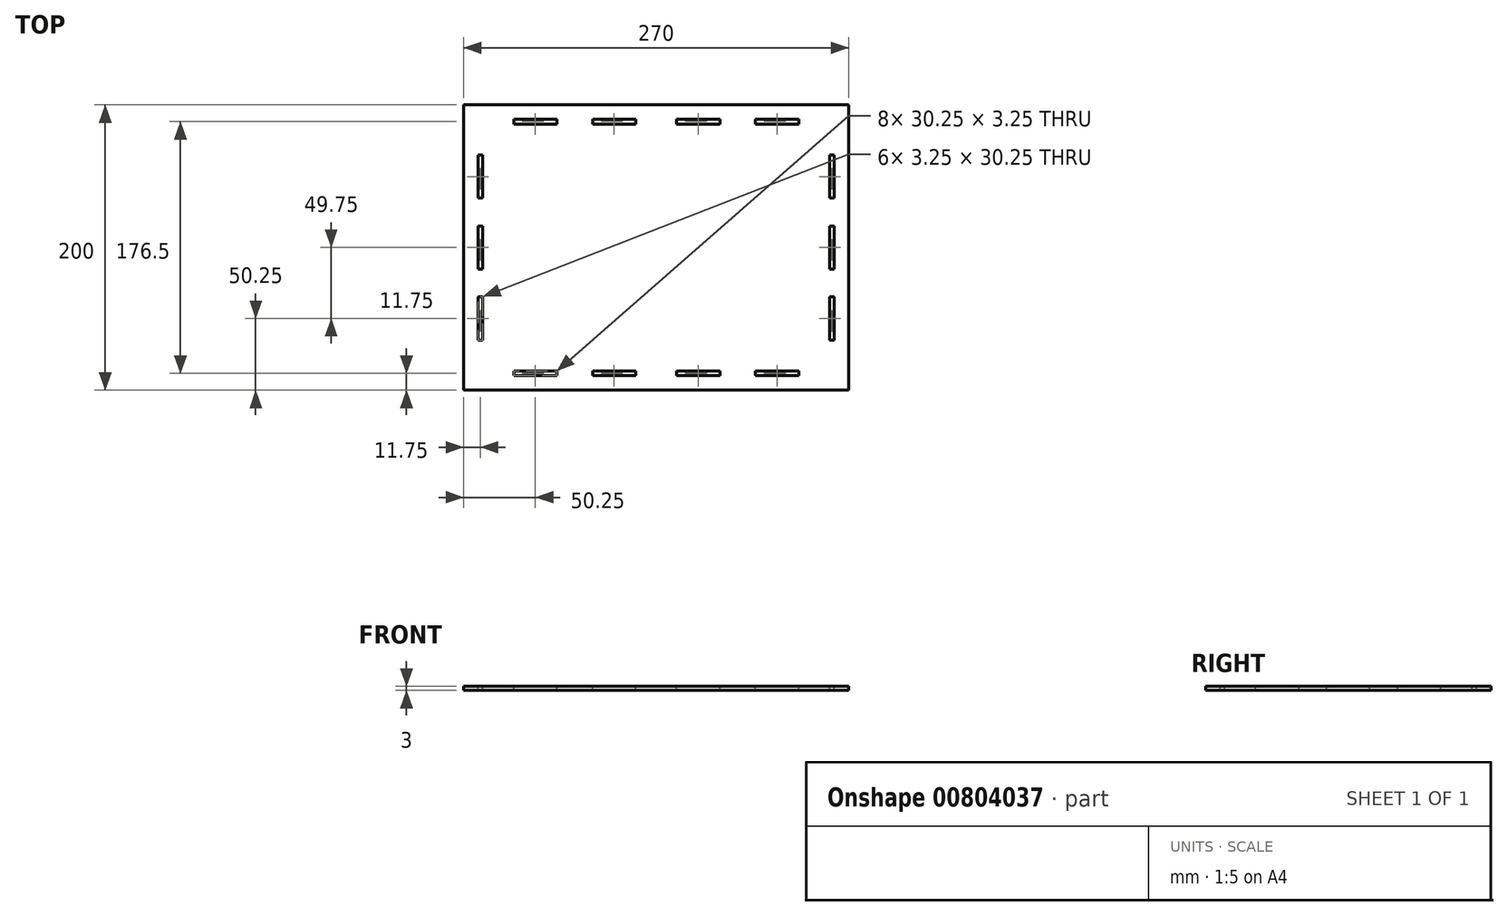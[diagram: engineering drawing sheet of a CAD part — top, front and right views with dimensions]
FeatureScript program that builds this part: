
annotation { "Feature Type Name" : "Feature", "Feature Type Description" : "" }
export const myFeature = defineFeature(function(context is Context, id is Id, definition is map)
    precondition{}
    {
        {
            var Q0;
            Q0=qCreatedBy(makeId("Top.planeOp"),FACE);
            var sketch = newSketch(context, id + "F0", { "sketchPlane" : qUnion([Q0])});
            skLineSegment(sketch, "E0.bottom", {"start": v(-135, 100) * mm, "end": v(135, 100) * mm});
            skLineSegment(sketch, "E0.top", {"start": v(-135, -100) * mm, "end": v(135, -100) * mm});
            skLineSegment(sketch, "E0.left", {"start": v(-135, 100) * mm, "end": v(-135, -100) * mm});
            skLineSegment(sketch, "E0.right", {"start": v(135, 100) * mm, "end": v(135, -100) * mm});
            skPoint(sketch, "E0.middle", {"position": v(0, 0) * mm});
            skSolve(sketch);
        }
        {
            var Q0;
            Q0=makeQuery(id+"F0.imprint","IMPRINT",FACE,{"disambiguationData":[TD([[makeQuery(id+"F0.imprint","IMPRINT",EDGE,{"derivedFrom":sQuery(id+"F0.wireOp",EDGE,"E0.bottom")}),-1.0]])]});
            extrude(context, id + "F1", {"entities" : qUnion([Q0]), "depth" : 3 * mm, "offsetDistance" : 25 * mm});
        }
        {
            var Q0;
            Q0=makeQuery(id+"F1.opExtrude","CAP_FACE",FACE,{"disambiguationData":[OSD([sQuery(id+"F0.wireOp",EDGE,"E0.bottom"),sQuery(id+"F0.wireOp",EDGE,"E0.top"),sQuery(id+"F0.wireOp",EDGE,"E0.left"),sQuery(id+"F0.wireOp",EDGE,"E0.right")])],"isStart":false});
            var sketch = newSketch(context, id + "F2", { "sketchPlane" : qUnion([Q0])});
            skLineSegment(sketch, "E1.bottom", {"start": v(-99.88, -86.63) * mm, "end": v(-69.63, -86.63) * mm});
            skLineSegment(sketch, "E1.top", {"start": v(-99.88, -89.88) * mm, "end": v(-69.63, -89.88) * mm});
            skLineSegment(sketch, "E1.left", {"start": v(-99.88, -86.63) * mm, "end": v(-99.88, -89.88) * mm});
            skLineSegment(sketch, "E1.right", {"start": v(-69.63, -86.63) * mm, "end": v(-69.63, -89.88) * mm});
            skPoint(sketch, "E1.middle", {"position": v(-84.75, -88.25) * mm});
            skLineSegment(sketch, "E2.bottom", {"start": v(-14.38, -86.62) * mm, "end": v(-44.63, -86.62) * mm});
            skLineSegment(sketch, "E2.top", {"start": v(-14.38, -89.88) * mm, "end": v(-44.63, -89.88) * mm});
            skLineSegment(sketch, "E2.left", {"start": v(-14.38, -86.62) * mm, "end": v(-14.38, -89.87) * mm});
            skLineSegment(sketch, "E2.right", {"start": v(-44.63, -86.62) * mm, "end": v(-44.63, -89.87) * mm});
            skPoint(sketch, "E2.middle", {"position": v(-29.5, -88.25) * mm});
            skLineSegment(sketch, "E3.bottom", {"start": v(121.63, 64.88) * mm, "end": v(124.88, 64.88) * mm});
            skLineSegment(sketch, "E3.top", {"start": v(121.63, 34.63) * mm, "end": v(124.88, 34.63) * mm});
            skLineSegment(sketch, "E3.left", {"start": v(121.63, 64.88) * mm, "end": v(121.63, 34.63) * mm});
            skLineSegment(sketch, "E3.right", {"start": v(124.88, 64.88) * mm, "end": v(124.88, 34.63) * mm});
            skPoint(sketch, "E3.middle", {"position": v(123.25, 49.75) * mm});
            skLineSegment(sketch, "E4.bottom", {"start": v(121.63, 15.12) * mm, "end": v(124.88, 15.12) * mm});
            skLineSegment(sketch, "E4.top", {"start": v(121.63, -15.13) * mm, "end": v(124.88, -15.13) * mm});
            skLineSegment(sketch, "E4.left", {"start": v(121.63, 15.12) * mm, "end": v(121.63, -15.13) * mm});
            skLineSegment(sketch, "E4.right", {"start": v(124.88, 15.12) * mm, "end": v(124.88, -15.13) * mm});
            skPoint(sketch, "E4.middle", {"position": v(123.25, 0) * mm});
            skLineSegment(sketch, "E5.MirrorCS", {"start": v(-69.63, 86.63) * mm, "end": v(-69.63, 89.88) * mm});
            skLineSegment(sketch, "E6.MirrorCS", {"start": v(-99.88, 86.63) * mm, "end": v(-99.88, 89.88) * mm});
            skLineSegment(sketch, "E7.MirrorCS", {"start": v(-44.63, 86.62) * mm, "end": v(-44.63, 89.87) * mm});
            skLineSegment(sketch, "E8.MirrorCS", {"start": v(-14.38, 86.62) * mm, "end": v(-14.38, 89.87) * mm});
            skLineSegment(sketch, "E9.MirrorCS", {"start": v(-14.38, 86.62) * mm, "end": v(-44.63, 86.62) * mm});
            skLineSegment(sketch, "E10.MirrorCS", {"start": v(-99.88, 89.88) * mm, "end": v(-69.63, 89.88) * mm});
            skLineSegment(sketch, "E11.MirrorCS", {"start": v(-99.88, 86.63) * mm, "end": v(-69.63, 86.63) * mm});
            skLineSegment(sketch, "E12.MirrorCS", {"start": v(-14.38, 89.88) * mm, "end": v(-44.63, 89.88) * mm});
            skPoint(sketch, "E13.MirrorP", {"position": v(-84.75, 88.25) * mm});
            skPoint(sketch, "E14.MirrorP", {"position": v(-29.5, 88.25) * mm});
            skLineSegment(sketch, "E15.MirrorCS", {"start": v(14.38, -86.62) * mm, "end": v(14.38, -89.87) * mm});
            skLineSegment(sketch, "E16.MirrorCS", {"start": v(69.63, -86.63) * mm, "end": v(69.63, -89.88) * mm});
            skLineSegment(sketch, "E17.MirrorCS", {"start": v(99.88, 86.63) * mm, "end": v(99.88, 89.88) * mm});
            skLineSegment(sketch, "E18.MirrorCS", {"start": v(14.38, 86.62) * mm, "end": v(14.38, 89.87) * mm});
            skLineSegment(sketch, "E19.MirrorCS", {"start": v(44.63, -86.62) * mm, "end": v(44.63, -89.87) * mm});
            skLineSegment(sketch, "E20.MirrorCS", {"start": v(99.88, -86.63) * mm, "end": v(99.88, -89.88) * mm});
            skLineSegment(sketch, "E21.MirrorCS", {"start": v(69.63, 86.63) * mm, "end": v(69.63, 89.88) * mm});
            skLineSegment(sketch, "E22.MirrorCS", {"start": v(44.63, 86.62) * mm, "end": v(44.63, 89.87) * mm});
            skLineSegment(sketch, "E23.MirrorCS", {"start": v(14.38, -89.88) * mm, "end": v(44.63, -89.88) * mm});
            skLineSegment(sketch, "E24.MirrorCS", {"start": v(99.88, -89.88) * mm, "end": v(69.63, -89.88) * mm});
            skLineSegment(sketch, "E25.MirrorCS", {"start": v(14.38, -86.62) * mm, "end": v(44.63, -86.62) * mm});
            skLineSegment(sketch, "E26.MirrorCS", {"start": v(14.38, 89.88) * mm, "end": v(44.63, 89.88) * mm});
            skLineSegment(sketch, "E27.MirrorCS", {"start": v(99.88, 89.88) * mm, "end": v(69.63, 89.88) * mm});
            skPoint(sketch, "E28.MirrorP", {"position": v(84.75, -88.25) * mm});
            skLineSegment(sketch, "E29.MirrorCS", {"start": v(99.88, 86.63) * mm, "end": v(69.63, 86.63) * mm});
            skLineSegment(sketch, "E30.MirrorCS", {"start": v(99.88, -86.63) * mm, "end": v(69.63, -86.63) * mm});
            skLineSegment(sketch, "E31.MirrorCS", {"start": v(14.38, 86.62) * mm, "end": v(44.63, 86.62) * mm});
            skPoint(sketch, "E32.MirrorP", {"position": v(84.75, 88.25) * mm});
            skPoint(sketch, "E33.MirrorP", {"position": v(29.5, 88.25) * mm});
            skPoint(sketch, "E34.MirrorP", {"position": v(29.5, -88.25) * mm});
            skLineSegment(sketch, "E35.MirrorCS", {"start": v(121.63, -34.63) * mm, "end": v(124.88, -34.63) * mm});
            skLineSegment(sketch, "E36.MirrorCS", {"start": v(121.63, -64.88) * mm, "end": v(124.88, -64.88) * mm});
            skLineSegment(sketch, "E37.MirrorCS", {"start": v(124.88, -64.88) * mm, "end": v(124.88, -34.63) * mm});
            skLineSegment(sketch, "E38.MirrorCS", {"start": v(121.63, -64.88) * mm, "end": v(121.63, -34.63) * mm});
            skPoint(sketch, "E39.MirrorP", {"position": v(123.25, -49.75) * mm});
            skLineSegment(sketch, "E40.MirrorCS", {"start": v(-121.63, -34.63) * mm, "end": v(-124.88, -34.63) * mm});
            skLineSegment(sketch, "E41.MirrorCS", {"start": v(-121.63, 34.63) * mm, "end": v(-124.88, 34.63) * mm});
            skLineSegment(sketch, "E42.MirrorCS", {"start": v(-121.63, -64.88) * mm, "end": v(-124.88, -64.88) * mm});
            skLineSegment(sketch, "E43.MirrorCS", {"start": v(-121.63, 15.12) * mm, "end": v(-124.88, 15.12) * mm});
            skLineSegment(sketch, "E44.MirrorCS", {"start": v(-121.63, 64.88) * mm, "end": v(-124.88, 64.88) * mm});
            skLineSegment(sketch, "E45.MirrorCS", {"start": v(-121.63, -15.13) * mm, "end": v(-124.88, -15.13) * mm});
            skPoint(sketch, "E46.MirrorP", {"position": v(-123.25, 49.75) * mm});
            skLineSegment(sketch, "E47.MirrorCS", {"start": v(-121.63, -64.88) * mm, "end": v(-121.63, -34.63) * mm});
            skPoint(sketch, "E48.MirrorP", {"position": v(-123.25, 0) * mm});
            skLineSegment(sketch, "E49.MirrorCS", {"start": v(-121.63, 64.88) * mm, "end": v(-121.63, 34.63) * mm});
            skPoint(sketch, "E50.MirrorP", {"position": v(-123.25, -49.75) * mm});
            skLineSegment(sketch, "E51.MirrorCS", {"start": v(-124.88, 15.12) * mm, "end": v(-124.88, -15.13) * mm});
            skLineSegment(sketch, "E52.MirrorCS", {"start": v(-121.63, 15.12) * mm, "end": v(-121.63, -15.13) * mm});
            skLineSegment(sketch, "E53.MirrorCS", {"start": v(-124.88, 64.88) * mm, "end": v(-124.88, 34.63) * mm});
            skLineSegment(sketch, "E54.MirrorCS", {"start": v(-124.88, -64.88) * mm, "end": v(-124.88, -34.63) * mm});
            skSolve(sketch);
        }
        {
            var Q0;
            Q0=qSketchRegion(id+"F2",true);
            extrude(context, id + "F3", {"entities" : qUnion([Q0]), "operationType" : NewBodyOperationType.REMOVE, "oppositeDirection" : true, "depth" : 3 * mm, "offsetDistance" : 25 * mm});
        }
    });
